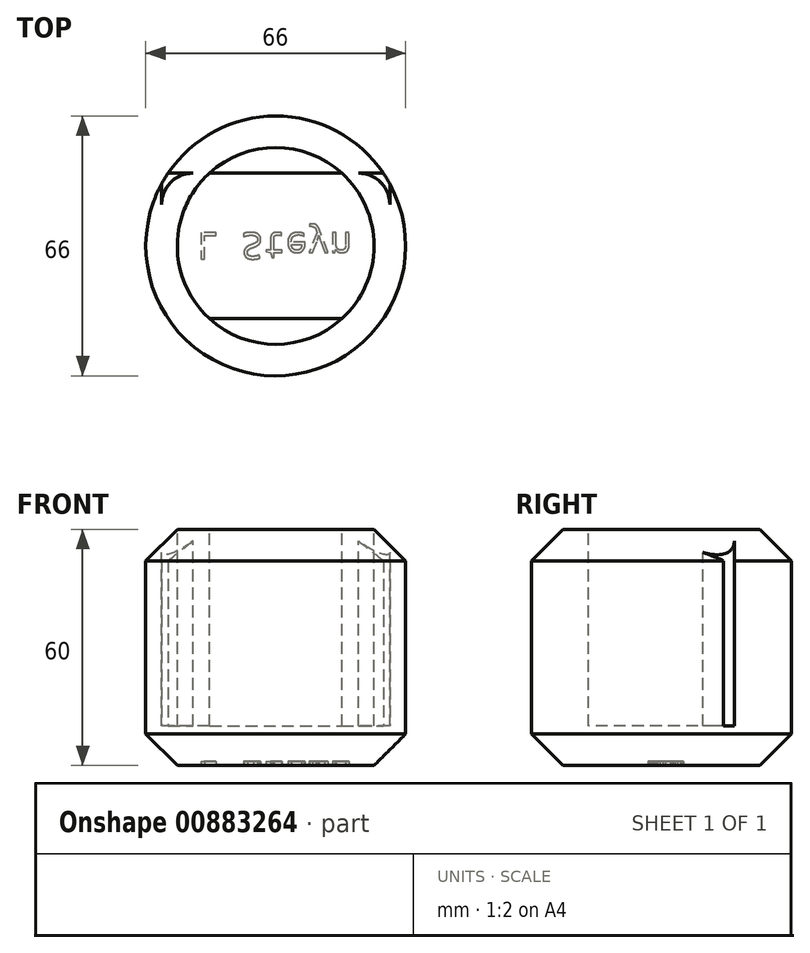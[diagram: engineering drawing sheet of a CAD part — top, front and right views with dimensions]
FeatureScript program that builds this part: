
annotation { "Feature Type Name" : "Feature", "Feature Type Description" : "" }
export const myFeature = defineFeature(function(context is Context, id is Id, definition is map)
    precondition{}
    {
        {
            var Q0;
            Q0=qCreatedBy(makeId("Top.planeOp"),FACE);
            var sketch = newSketch(context, id + "F0", { "sketchPlane" : qUnion([Q0])});
            skCircle(sketch, "E0", {"center": v(0, 0) * mm, "radius": 33 * mm});
            skSolve(sketch);
        }
        {
            var Q0;
            Q0=makeQuery(id+"F0.imprint","IMPRINT",FACE,{"disambiguationData":[TD([[makeQuery(id+"F0.imprint","IMPRINT",EDGE,{"derivedFrom":sQuery(id+"F0.wireOp",EDGE,"E0")}),1.0]])]});
            extrude(context, id + "F1", {"entities" : qUnion([Q0]), "depth" : 60 * mm, "offsetDistance" : 25 * mm});
        }
        {
            var Q0;
            Q0=makeQuery(id+"F1.opExtrude","CAP_EDGE",EDGE,{"disambiguationData":[OSD([sQuery(id+"F0.wireOp",EDGE,"E0")])],"isStart":true});
            var Q1;
            Q1=makeQuery(id+"F1.opExtrude","CAP_EDGE",EDGE,{"disambiguationData":[OSD([sQuery(id+"F0.wireOp",EDGE,"E0")])],"isStart":false});
            chamfer(context, id + "F2", {"entities" : qUnion([Q0, Q1]), "width" : 8 * mm, "tangentPropagation" : true});
        }
        {
            var Q0;
            Q0=makeQuery(id+"F1.opExtrude","CAP_FACE",FACE,{"disambiguationData":[OSD([sQuery(id+"F0.wireOp",EDGE,"E0")])],"isStart":false});
            var sketch = newSketch(context, id + "F3", { "sketchPlane" : qUnion([Q0])});
            skLineSegment(sketch, "E1.bottom", {"start": v(-29, 18.5) * mm, "end": v(29, 18.5) * mm});
            skLineSegment(sketch, "E1.top", {"start": v(-29, -18.5) * mm, "end": v(29, -18.5) * mm});
            skLineSegment(sketch, "E1.left", {"start": v(-29, 18.5) * mm, "end": v(-29, -18.5) * mm});
            skLineSegment(sketch, "E1.right", {"start": v(29, 18.5) * mm, "end": v(29, -18.5) * mm});
            skPoint(sketch, "E2", {"position": v(-21, 10.5) * mm});
            skPoint(sketch, "E3", {"position": v(21, 10.5) * mm});
            skPoint(sketch, "E4", {"position": v(21, -10.5) * mm});
            skPoint(sketch, "E5", {"position": v(-21, -10.5) * mm});
            skArc(sketch, "E6", {"start": v(-29, 10.5) * mm, "mid": v(-26.66, 16.16) * mm, "end": v(-21, 18.5) * mm});
            skArc(sketch, "E7", {"start": v(21, 18.5) * mm, "mid": v(26.66, 16.16) * mm, "end": v(29, 10.5) * mm});
            skArc(sketch, "E8", {"start": v(29, -10.5) * mm, "mid": v(26.66, -16.16) * mm, "end": v(21, -18.5) * mm});
            skArc(sketch, "E9", {"start": v(-21, -18.5) * mm, "mid": v(-26.66, -16.16) * mm, "end": v(-29, -10.5) * mm});
            skSolve(sketch);
        }
        {
            var Q0;
            {var subQ0=sQuery(id+"F3.wireOp",EDGE,"E1.bottom");var subQ1=sQuery(id+"F0.wireOp",EDGE,"E0");var subQ2=makeQuery(id+"F2.opChamfer","BLEND_EDGE",EDGE,{"blendedFrom":[makeQuery(id+"F1.opExtrude","CAP_EDGE",EDGE,{"disambiguationData":[OSD([subQ1])],"isStart":false}),makeQuery(id+"F1.opExtrude","CAP_FACE",FACE,{"disambiguationData":[OSD([subQ1])],"isStart":false})],"blendedInto":[makeQuery(id+"F1.opExtrude","CAP_FACE",FACE,{"disambiguationData":[OSD([subQ1])],"isStart":false})]});var subQ3=makeQuery(id+"F3.imprint","INTERSECT",VERTEX,{"disambiguationData":[OD(0.0)],"derivedFrom":[subQ2,subQ0]});Q0=makeQuery(id+"F3.imprint","IMPRINT",FACE,{"disambiguationData":[TD([[makeQuery(id+"F3.imprint","IMPRINT",EDGE,{"disambiguationData":[TD([[subQ3,-1.0]])],"derivedFrom":subQ0}),-1.0]])]});}
            var Q1;
            {var subQ0=sQuery(id+"F3.wireOp",EDGE,"E6");Q1=makeQuery(id+"F3.imprint","IMPRINT",FACE,{"disambiguationData":[TD([[makeQuery(id+"F3.imprint","IMPRINT",EDGE,{"derivedFrom":subQ0}),-1.0]])]});}
            var Q2;
            {var subQ0=sQuery(id+"F3.wireOp",EDGE,"E7");Q2=makeQuery(id+"F3.imprint","IMPRINT",FACE,{"disambiguationData":[TD([[makeQuery(id+"F3.imprint","IMPRINT",EDGE,{"derivedFrom":subQ0}),-1.0]])]});}
            extrude(context, id + "F4", {"entities" : qUnion([Q0, Q1, Q2]), "operationType" : NewBodyOperationType.REMOVE, "oppositeDirection" : true, "depth" : 50 * mm, "offsetDistance" : 25 * mm});
        }
        {
            var Q0;
            Q0=makeQuery(id+"F1.opExtrude","CAP_FACE",FACE,{"disambiguationData":[OSD([sQuery(id+"F0.wireOp",EDGE,"E0")])],"isStart":true});
            var sketch = newSketch(context, id + "F5", { "sketchPlane" : qUnion([Q0])});
            skText(sketch, "E10", { "text": "L Steyn", "fontName": "DroidSansMono.ttf"});
            const initialGuessF5  = {"E10": [-0.02, -0.00337, 1, 0, 0.00674]};
            skSetInitialGuess(sketch, initialGuessF5);
            skSolve(sketch);
        }
        {
            var Q0;
            Q0 = qSketchRegion(id + "F5", true);
            extrude(context, id + "F6", {"entities" : qUnion([Q0]), "operationType" : NewBodyOperationType.REMOVE, "oppositeDirection" : true, "depth" : 1 * mm, "offsetDistance" : 25 * mm});
        }
    });
